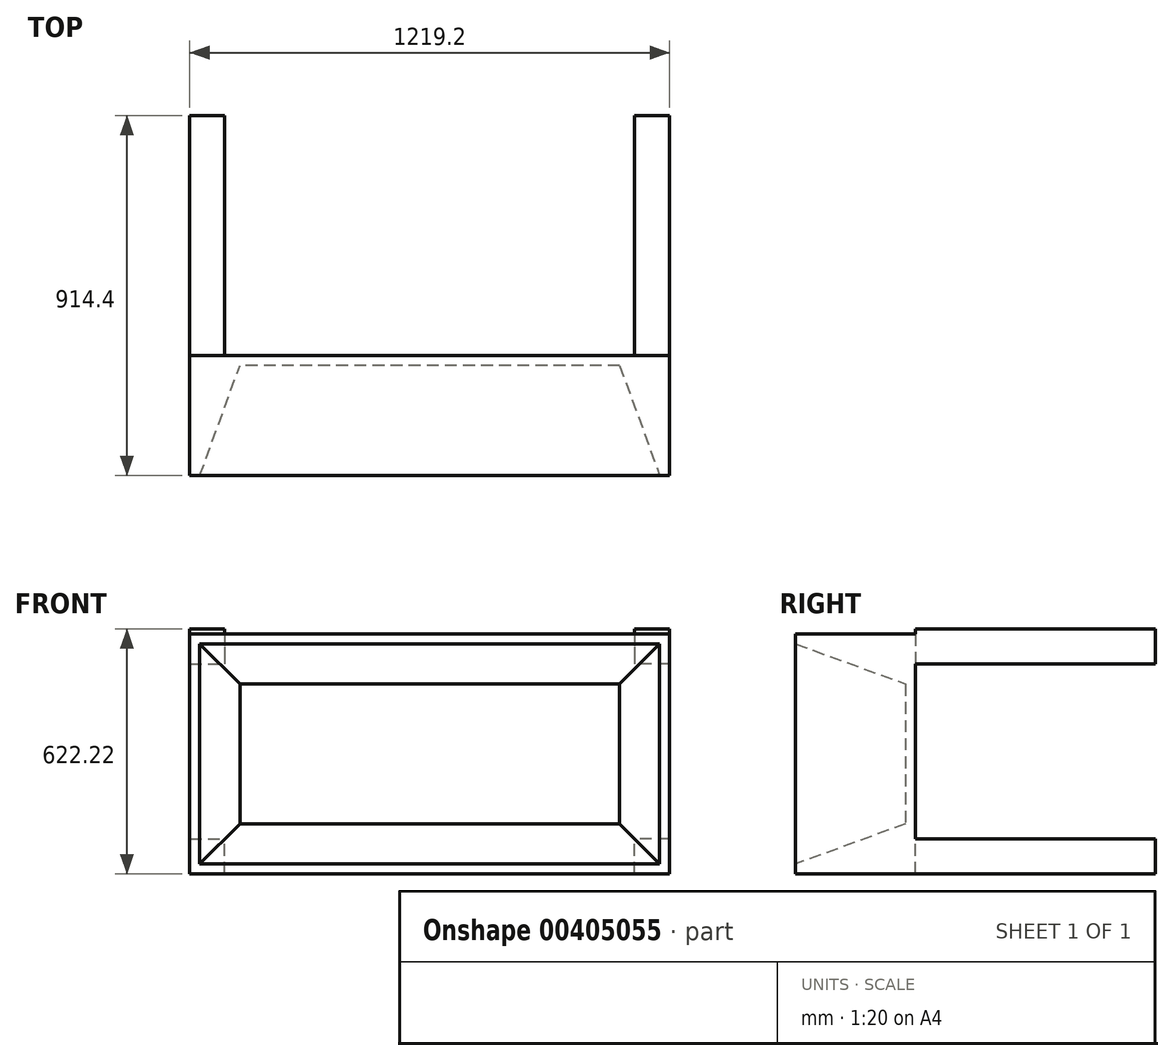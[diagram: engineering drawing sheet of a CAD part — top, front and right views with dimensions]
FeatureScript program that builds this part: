
annotation { "Feature Type Name" : "Feature", "Feature Type Description" : "" }
export const myFeature = defineFeature(function(context is Context, id is Id, definition is map)
    precondition{}
    {
        {
            var Q0;
            Q0=qCreatedBy(makeId("Front.planeOp"),FACE);
            var sketch = newSketch(context, id + "F0", { "sketchPlane" : qUnion([Q0])});
            skLineSegment(sketch, "E0.bottom", {"start": v(-609.6, 214.7) * mm, "end": v(609.6, 214.7) * mm});
            skLineSegment(sketch, "E0.top", {"start": v(-609.6, -394.9) * mm, "end": v(609.6, -394.9) * mm});
            skLineSegment(sketch, "E0.left", {"start": v(-609.6, 214.7) * mm, "end": v(-609.6, -394.9) * mm});
            skLineSegment(sketch, "E0.right", {"start": v(609.6, 214.7) * mm, "end": v(609.6, -394.9) * mm});
            skSolve(sketch);
        }
        {
            var Q0;
            Q0 = qSketchRegion(id + "F0", true);
            extrude(context, id + "F1", {"entities" : qUnion([Q0]), "depth" : 304.8 * mm});
        }
        {
            var Q0;
            Q0=makeQuery(id+"F1.opExtrude","CAP_FACE",FACE,{"disambiguationData":[OSD([sQuery(id+"F0.wireOp",EDGE,"E0.bottom"),sQuery(id+"F0.wireOp",EDGE,"E0.top"),sQuery(id+"F0.wireOp",EDGE,"E0.left"),sQuery(id+"F0.wireOp",EDGE,"E0.right")])],"isStart":false});
            var sketch = newSketch(context, id + "F2", { "sketchPlane" : qUnion([Q0])});
            skLineSegment(sketch, "E1.bottom", {"start": v(-584.2, 189.3) * mm, "end": v(584.2, 189.3) * mm});
            skLineSegment(sketch, "E1.top", {"start": v(-584.2, -369.5) * mm, "end": v(584.2, -369.5) * mm});
            skLineSegment(sketch, "E1.left", {"start": v(-584.2, 189.3) * mm, "end": v(-584.2, -369.5) * mm});
            skLineSegment(sketch, "E1.right", {"start": v(584.2, 189.3) * mm, "end": v(584.2, -369.5) * mm});
            skSolve(sketch);
        }
        {
            var Q0;
            Q0=makeQuery(id+"F2.imprint","IMPRINT",FACE,{"disambiguationData":[TD([[makeQuery(id+"F2.imprint","IMPRINT",EDGE,{"derivedFrom":sQuery(id+"F2.wireOp",EDGE,"E1.bottom")}),-1.0]])]});
            extrude(context, id + "F3", {"entities" : qUnion([Q0]), "operationType" : NewBodyOperationType.REMOVE, "oppositeDirection" : true, "depth" : 279.4 * mm, "hasDraft" : true, "draftAngle" : 20 * degree, "draftPullDirection" : true});
        }
        {
            var Q0;
            Q0=makeQuery(id+"F0.imprint","IMPRINT",FACE,{"disambiguationData":[TD([[makeQuery(id+"F0.imprint","IMPRINT",EDGE,{"derivedFrom":sQuery(id+"F0.wireOp",EDGE,"E0.bottom")}),-1.0]])]});
            var sketch = newSketch(context, id + "F4", { "sketchPlane" : qUnion([Q0])});
            skLineSegment(sketch, "E2", {"start": v(0, -394.54) * mm, "end": v(0, 216.12) * mm});
            skLineSegment(sketch, "E3.bottom", {"start": v(-609.6, -394.9) * mm, "end": v(-520.7, -394.9) * mm});
            skLineSegment(sketch, "E3.top", {"start": v(-609.6, -306) * mm, "end": v(-520.7, -306) * mm});
            skLineSegment(sketch, "E3.left", {"start": v(-609.6, -394.9) * mm, "end": v(-609.6, -306) * mm});
            skLineSegment(sketch, "E3.right", {"start": v(-520.7, -394.9) * mm, "end": v(-520.7, -306) * mm});
            skLineSegment(sketch, "E4.MirrorCS", {"start": v(520.7, -394.9) * mm, "end": v(520.7, -306) * mm});
            skLineSegment(sketch, "E5.MirrorCS", {"start": v(609.6, -306) * mm, "end": v(520.7, -306) * mm});
            skLineSegment(sketch, "E6.MirrorCS", {"start": v(609.6, -394.9) * mm, "end": v(520.7, -394.9) * mm});
            skLineSegment(sketch, "E7.MirrorCS", {"start": v(609.6, -394.9) * mm, "end": v(609.6, -306) * mm});
            skLineSegment(sketch, "E8", {"start": v(-612.72, -83.8) * mm, "end": v(608.6, -83.8) * mm});
            skLineSegment(sketch, "E9.MirrorCS", {"start": v(609.6, 227.32) * mm, "end": v(520.7, 227.32) * mm});
            skLineSegment(sketch, "E10.MirrorCS", {"start": v(520.7, 227.32) * mm, "end": v(520.7, 138.42) * mm});
            skLineSegment(sketch, "E11.MirrorCS", {"start": v(609.6, 138.42) * mm, "end": v(520.7, 138.42) * mm});
            skLineSegment(sketch, "E12.MirrorCS", {"start": v(609.6, 227.32) * mm, "end": v(609.6, 138.42) * mm});
            skLineSegment(sketch, "E13.MirrorCS", {"start": v(-520.7, 227.32) * mm, "end": v(-520.7, 138.42) * mm});
            skLineSegment(sketch, "E14.MirrorCS", {"start": v(-609.6, 138.42) * mm, "end": v(-520.7, 138.42) * mm});
            skLineSegment(sketch, "E15.MirrorCS", {"start": v(-609.6, 227.32) * mm, "end": v(-609.6, 138.42) * mm});
            skLineSegment(sketch, "E16.MirrorCS", {"start": v(-609.6, 227.32) * mm, "end": v(-520.7, 227.32) * mm});
            skSolve(sketch);
        }
        {
            var Q0;
            Q0 = qSketchRegion(id + "F4", true);
            extrude(context, id + "F5", {"entities" : qUnion([Q0]), "operationType" : NewBodyOperationType.ADD, "oppositeDirection" : true, "depth" : 609.6 * mm});
        }
    });
